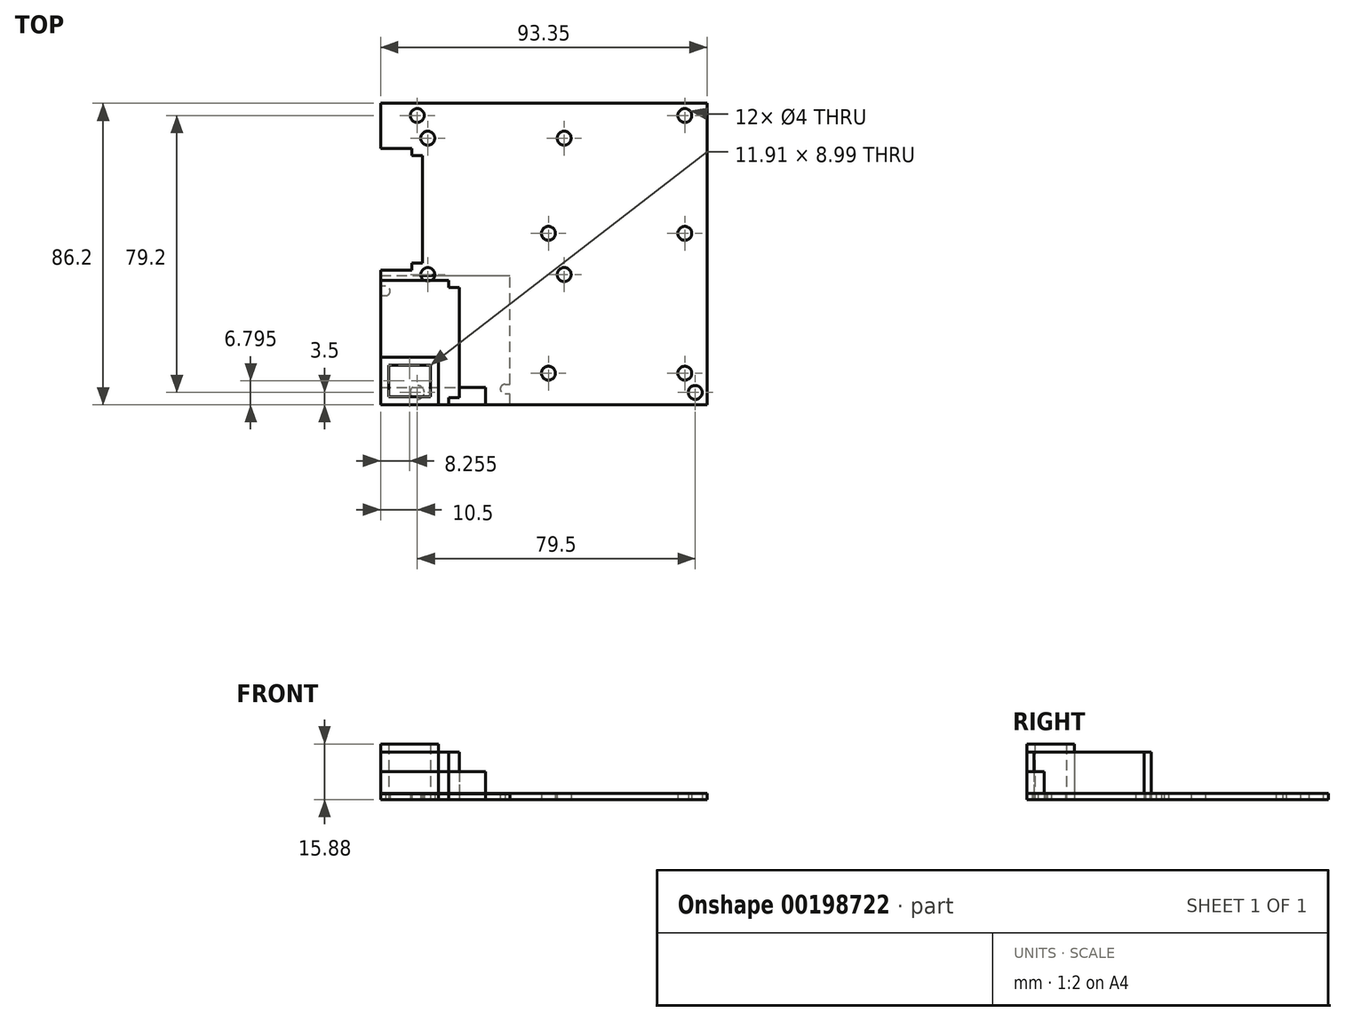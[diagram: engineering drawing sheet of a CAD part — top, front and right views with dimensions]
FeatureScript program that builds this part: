
annotation { "Feature Type Name" : "Feature", "Feature Type Description" : "" }
export const myFeature = defineFeature(function(context is Context, id is Id, definition is map)
    precondition{}
    {
        {
            var Q0;
            Q0=qCreatedBy(makeId("Top.planeOp"),FACE);
            var sketch = newSketch(context, id + "F0", { "sketchPlane" : qUnion([Q0])});
            skLineSegment(sketch, "E0.bottom", {"start": v(0, 0) * mm, "end": v(37, 0) * mm});
            skLineSegment(sketch, "E0.top", {"start": v(0, 37) * mm, "end": v(37, 37) * mm});
            skLineSegment(sketch, "E0.left", {"start": v(0, 0) * mm, "end": v(0, 37) * mm});
            skLineSegment(sketch, "E0.right", {"start": v(37, 0) * mm, "end": v(37, 37) * mm});
            skArc(sketch, "E1", {"start": v(1.39, 31.15) * mm, "mid": v(2.75, 32.5) * mm, "end": v(1.39, 33.85) * mm});
            skArc(sketch, "E2", {"start": v(35.61, 5.85) * mm, "mid": v(34.25, 4.49) * mm, "end": v(35.64, 3.15) * mm});
            skLineSegment(sketch, "E3", {"start": v(35.59, 5.85) * mm, "end": v(37, 5.85) * mm});
            skLineSegment(sketch, "E4", {"start": v(35.56, 3.15) * mm, "end": v(37, 3.15) * mm});
            skLineSegment(sketch, "E5", {"start": v(1.39, 33.85) * mm, "end": v(0, 33.85) * mm});
            skLineSegment(sketch, "E6", {"start": v(1.39, 31.15) * mm, "end": v(0, 31.15) * mm});
            skSolve(sketch);
        }
        {
            var Q0;
            {var subQ9=sQuery(id+"F0.wireOp",EDGE,"E0.bottom");Q0=makeQuery(id+"F0.imprint","IMPRINT",FACE,{"disambiguationData":[TD([[makeQuery(id+"F0.imprint","IMPRINT",EDGE,{"derivedFrom":subQ9}),1.0]])]});}
            extrude(context, id + "F1", {"entities" : qUnion([Q0]), "depth" : 1.6 * mm, "offsetDistance" : 25 * mm});
        }
        {
            var Q0;
            Q0=qCreatedBy(makeId("Top.planeOp"),FACE);
            var sketch = newSketch(context, id + "F2", { "sketchPlane" : qUnion([Q0])});
            skLineSegment(sketch, "E7.bottom", {"start": v(0, 0) * mm, "end": v(30, 0) * mm});
            skLineSegment(sketch, "E7.top", {"start": v(0, 5) * mm, "end": v(30, 5) * mm});
            skLineSegment(sketch, "E7.left", {"start": v(0, 0) * mm, "end": v(0, 5) * mm});
            skLineSegment(sketch, "E7.right", {"start": v(30, 0) * mm, "end": v(30, 5) * mm});
            skSolve(sketch);
        }
        {
            var Q0;
            Q0 = qSketchRegion(id + "F2", true);
            extrude(context, id + "F3", {"entities" : qUnion([Q0]), "depth" : 8 * mm, "offsetDistance" : 25 * mm});
        }
        {
            var Q0;
            Q0=qCreatedBy(makeId("Top.planeOp"),FACE);
            var sketch = newSketch(context, id + "F4", { "sketchPlane" : qUnion([Q0])});
            skLineSegment(sketch, "E8.bottom", {"start": v(0, 0) * mm, "end": v(93.35, 0) * mm});
            skLineSegment(sketch, "E8.top", {"start": v(0, 86.2) * mm, "end": v(93.35, 86.2) * mm});
            skLineSegment(sketch, "E8.left", {"start": v(0, 0) * mm, "end": v(0, 38.5) * mm});
            skLineSegment(sketch, "E8.right", {"start": v(93.35, 0) * mm, "end": v(93.35, 86.2) * mm});
            skCircle(sketch, "E9", {"center": v(10.5, 3.5) * mm, "radius": 2 * mm});
            skCircle(sketch, "E10", {"center": v(13.5, 76.2) * mm, "radius": 2 * mm});
            skCircle(sketch, "E11", {"center": v(48, 49) * mm, "radius": 2 * mm});
            skCircle(sketch, "E12", {"center": v(52.5, 76.2) * mm, "radius": 2 * mm});
            skCircle(sketch, "E13", {"center": v(52.5, 37.2) * mm, "radius": 2 * mm});
            skCircle(sketch, "E14", {"center": v(87, 49) * mm, "radius": 2 * mm});
            skCircle(sketch, "E15", {"center": v(48, 9) * mm, "radius": 2 * mm});
            skCircle(sketch, "E16", {"center": v(87, 9) * mm, "radius": 2 * mm});
            skCircle(sketch, "E17", {"center": v(90, 3.5) * mm, "radius": 2 * mm});
            skCircle(sketch, "E18", {"center": v(10.5, 82.7) * mm, "radius": 2 * mm});
            skCircle(sketch, "E19", {"center": v(87, 82.7) * mm, "radius": 2 * mm});
            skCircle(sketch, "E20", {"center": v(13.5, 37.2) * mm, "radius": 2 * mm});
            skLineSegment(sketch, "E21.bottom", {"start": v(0, 73.2) * mm, "end": v(9, 73.2) * mm});
            skLineSegment(sketch, "E21.top", {"start": v(0, 38.5) * mm, "end": v(9, 38.5) * mm});
            skLineSegment(sketch, "E21.right", {"start": v(12, 71.2) * mm, "end": v(12, 40.5) * mm});
            skLineSegment(sketch, "E22.top", {"start": v(12, 71.2) * mm, "end": v(9, 71.2) * mm});
            skLineSegment(sketch, "E22.right", {"start": v(9, 73.2) * mm, "end": v(9, 71.2) * mm});
            skLineSegment(sketch, "E23.bottom", {"start": v(12, 38.5) * mm, "end": v(11.98, 38.5) * mm});
            skLineSegment(sketch, "E23.top", {"start": v(12, 40.5) * mm, "end": v(9, 40.5) * mm});
            skLineSegment(sketch, "E23.left", {"start": v(12, 38.5) * mm, "end": v(12, 38.52) * mm});
            skLineSegment(sketch, "E23.right", {"start": v(9, 38.5) * mm, "end": v(9, 40.5) * mm});
            skLineSegment(sketch, "E24.trimOffspring", {"start": v(11.98, 38.5) * mm, "end": v(12, 38.5) * mm});
            skLineSegment(sketch, "E25.trimOffspring", {"start": v(12, 38.52) * mm, "end": v(12, 38.5) * mm});
            skLineSegment(sketch, "E26.trimOffspring", {"start": v(0, 73.2) * mm, "end": v(0, 86.2) * mm});
            skSolve(sketch);
        }
        {
            var Q0;
            Q0 = qSketchRegion(id + "F4", true);
            extrude(context, id + "F5", {"entities" : qUnion([Q0]), "depth" : 1.8 * mm, "offsetDistance" : 25 * mm});
        }
        {
            var Q0;
            Q0=qCreatedBy(makeId("Top.planeOp"),FACE);
            var sketch = newSketch(context, id + "F6", { "sketchPlane" : qUnion([Q0])});
            skLineSegment(sketch, "E27.bottom", {"start": v(0, 0) * mm, "end": v(19.5, 0) * mm});
            skLineSegment(sketch, "E27.top", {"start": v(0, 35.5) * mm, "end": v(19.5, 35.5) * mm});
            skLineSegment(sketch, "E27.left", {"start": v(0, 0) * mm, "end": v(0, 35.5) * mm});
            skLineSegment(sketch, "E27.right", {"start": v(22.5, 2) * mm, "end": v(22.5, 33.5) * mm});
            skLineSegment(sketch, "E28.top", {"start": v(22.5, 33.5) * mm, "end": v(19.5, 33.5) * mm});
            skLineSegment(sketch, "E28.right", {"start": v(19.5, 35.5) * mm, "end": v(19.5, 33.5) * mm});
            skLineSegment(sketch, "E29.top", {"start": v(22.5, 2) * mm, "end": v(19.5, 2) * mm});
            skLineSegment(sketch, "E29.right", {"start": v(19.5, 0) * mm, "end": v(19.5, 2) * mm});
            skSolve(sketch);
        }
        {
            var Q0;
            Q0 = qSketchRegion(id + "F6", true);
            extrude(context, id + "F7", {"entities" : qUnion([Q0]), "depth" : 13.5 * mm, "offsetDistance" : 25 * mm});
        }
        {
            var Q0;
            Q0=qCreatedBy(makeId("Top.planeOp"),FACE);
            var sketch = newSketch(context, id + "F8", { "sketchPlane" : qUnion([Q0])});
            skLineSegment(sketch, "E30.bottom", {"start": v(0, 0) * mm, "end": v(16.51, 0) * mm});
            skLineSegment(sketch, "E30.top", {"start": v(0, 13.59) * mm, "end": v(16.51, 13.59) * mm});
            skLineSegment(sketch, "E30.left", {"start": v(0, 0) * mm, "end": v(0, 13.59) * mm});
            skLineSegment(sketch, "E30.right", {"start": v(16.51, 0) * mm, "end": v(16.51, 13.59) * mm});
            skLineSegment(sketch, "E31.0", {"start": v(2.3, 2.3) * mm, "end": v(2.3, 11.29) * mm});
            skLineSegment(sketch, "E31.1", {"start": v(2.3, 2.3) * mm, "end": v(14.2, 2.3) * mm});
            skLineSegment(sketch, "E31.2", {"start": v(14.2, 2.3) * mm, "end": v(14.2, 11.29) * mm});
            skLineSegment(sketch, "E31.3", {"start": v(2.3, 11.29) * mm, "end": v(14.2, 11.29) * mm});
            skSolve(sketch);
        }
        {
            var Q0;
            Q0=makeQuery(id+"F8.imprint","IMPRINT",FACE,{"disambiguationData":[TD([[makeQuery(id+"F8.imprint","IMPRINT",EDGE,{"derivedFrom":sQuery(id+"F8.wireOp",EDGE,"E30.bottom")}),1.0]])]});
            var Q1;
            Q1 = qConstructionFilter(qBodyType(qCreatedBy(id + "F8" ,EDGE), BodyType.WIRE), ConstructionObject.NO);
            extrude(context, id + "F9", {"entities" : qUnion([Q0]), "surfaceEntities" : qUnion([Q1]), "depth" : 15.88 * mm, "offsetDistance" : 25 * mm});
        }
    });
